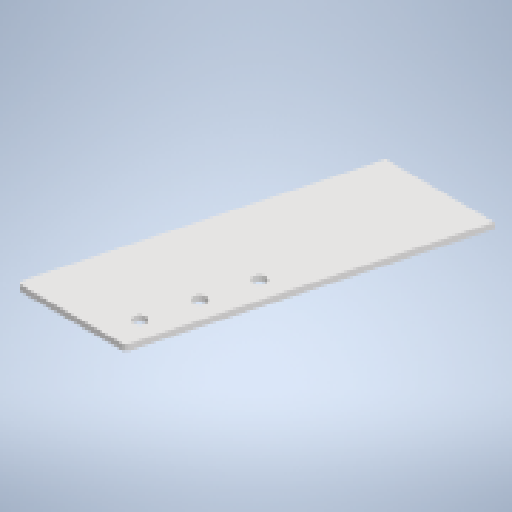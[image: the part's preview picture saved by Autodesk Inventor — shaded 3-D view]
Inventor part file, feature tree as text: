
AUTODESK INVENTOR PART (.ipt)
format: ipt  version: 2024.2 (Build 282272000, 272)  size: 286,720 bytes
history: native  units: mm
features: sketch x3, sheet_metal_op x1, hole x1, chamfer x1, extrude x1, fillet x1, other x1, projected_geometry x1
ambient origin geometry x8: Origin, YZ Plane, XZ Plane, XY Plane, X Axis, Y Axis, Z Axis, Center Point
bodies: Solid1 (feature_tree)
feature tree (10):
  sheet_metal_op  "Face1"
  hole  "Hole1"  [1 undecoded]
  chamfer  "Corner Round1"
  extrude  "Extrusion1"  Depth=195.0mm
  fillet  "Fillet1"  Radius=6.0mm
  sketch  "Sketch1"  dims[d1=200.0mm d2=15.0deg]
  other  "Plate1"
  sketch  "Sketch3"  dims[d3=8.0mm]
  sketch  "Sketch5"  dims[d4=17.0mm d5=6.0mm d6=4.0mm d7=2.0mm d8=90.0deg d9=8.0mm d10=20.594885mm d14=6.0mm d28=135.0mm d29=160.0mm d30=14.0mm d31=45.0mm d32=17.104227mm d33=0.0mm d34=0.0mm d35=2.0mm d36=90.0mm d37=255.0mm d38=195.0mm d39=60.0mm]
  projected_geometry  "Projected Loop2"
note: 1 required parameter value undecoded (feature->parameter linkage not recoverable at this tier; creation-order binding heuristic only, values carry confidence <= 0.55)
